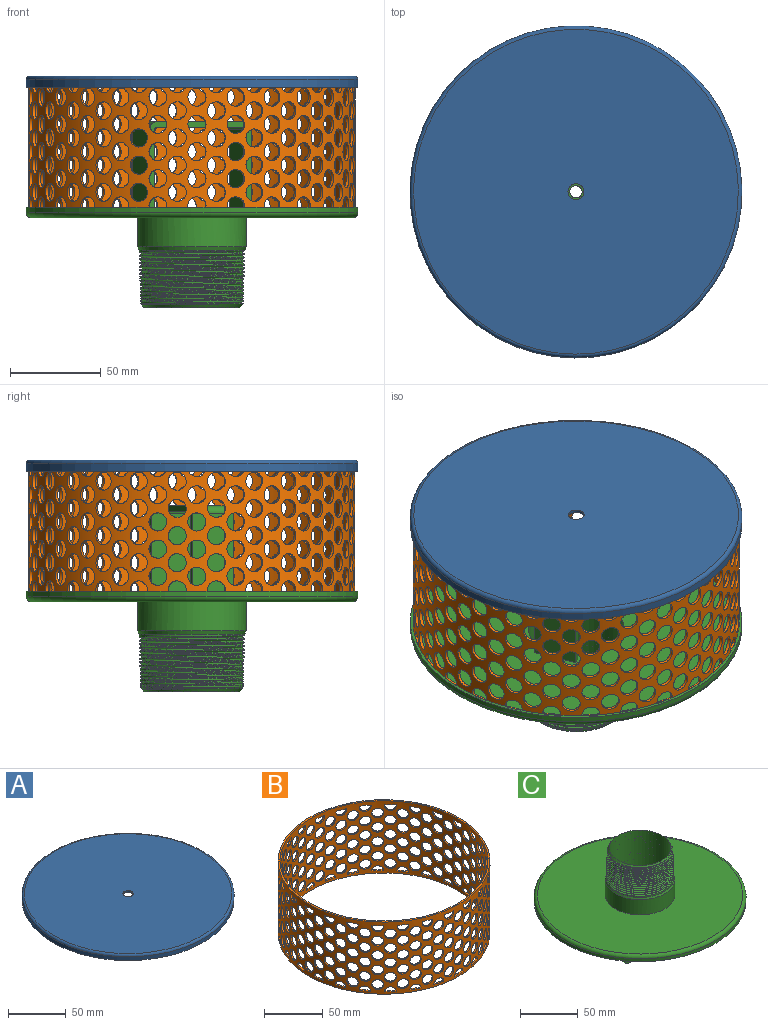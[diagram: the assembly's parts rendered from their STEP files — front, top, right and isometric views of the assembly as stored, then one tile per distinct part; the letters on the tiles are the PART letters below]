
ASSEMBLY  parts=3 mates=4
PART A: 8 faces, bbox 198.3x198.3x6 mm
  f0: cylinder r=91.6mm len=183.2mm, axis (0,0,-1), area 2302.2mm2, adj f2,f3
  f1: plane 179.2x179.2mm, normal (0,0,1), area 25160.4mm2, adj f3,f7
  f2: plane 183.2x183.2mm, normal (0,0,-1), area 912.8mm2, adj f0,f4
  f3: torus R=89.6mm, axis (0,0,1), area 1793.8mm2, adj f0,f1
  f4: cylinder r=90mm len=180mm, axis (0,0,-1), area 2261.9mm2, adj f2,f6
  f5: plane 179.2x179.2mm, normal (0,0,-1), area 25160.4mm2, adj f6,f7
  f6: torus R=89.6mm, axis (0,0,1), area 354.7mm2, adj f4,f5
  f7: cylinder r=4.4mm len=8.8mm, axis (0,0,1), area 44.2mm2, adj f1,f5
PART B: 316 faces, bbox 180x180x75 mm
  f0: cylinder r=90mm len=180mm, axis (0,0,-1), area 23634.4mm2, adj f2,f3,f4,f5,f6,f7,f8,f9
  f1: cylinder r=88.4mm len=176.8mm, axis (0,0,-1), area 22883mm2, adj f2,f3,f4,f5,f6,f7,f8,f9
  f2: plane 180x180mm, normal (0,0,1), area 896.7mm2, adj f0,f1
  f3: plane 180x180mm, normal (0,0,-1), area 896.7mm2, adj f0,f1
  f4: cylinder r=5mm len=10mm, axis (-1,0,0), area 50.3mm2, adj f0,f1
  f5: cylinder r=5mm len=10mm, axis (-1,0,0), area 28.9mm2, adj f0,f1,f6
  f6: plane 9.76x1.74mm, normal (0,0,-1), area 15.6mm2, adj f0,f1,f5
  f7: cylinder r=5mm len=10mm, axis (-1,0,0), area 50.3mm2, adj f0,f1
  f8: cylinder r=5mm len=10mm, axis (-1,0,0), area 50.3mm2, adj f0,f1
  f9: cylinder r=5mm len=10mm, axis (-1,0,0), area 50.3mm2, adj f0,f1
  f10: cylinder r=5mm len=10.13mm, axis (-0.97,-0.24,0), area 50.3mm2, adj f0,f1
  f11: cylinder r=5mm len=10.13mm, axis (-0.97,-0.24,0), area 28.7mm2, adj f0,f1,f12
  f12: plane 9.86x3.89mm, normal (0,0,-1), area 15.6mm2, adj f0,f1,f11
  f13: cylinder r=5mm len=10.13mm, axis (-0.97,-0.24,0), area 50.3mm2, adj f0,f1
  f14: cylinder r=5mm len=10.13mm, axis (-0.97,-0.24,0), area 50.3mm2, adj f0,f1
  f15: cylinder r=5mm len=10.13mm, axis (-0.97,-0.24,0), area 50.3mm2, adj f0,f1
  f16: cylinder r=5mm len=10mm, axis (-0.89,-0.46,0), area 50.3mm2, adj f0,f1
  f17: cylinder r=5mm len=9.66mm, axis (-0.89,-0.46,0), area 28.7mm2, adj f0,f1,f18
  f18: plane 9.39x5.96mm, normal (0,0,-1), area 15.6mm2, adj f0,f1,f17
  f19: cylinder r=5mm len=10mm, axis (-0.89,-0.46,0), area 50.3mm2, adj f0,f1
  f20: cylinder r=5mm len=10mm, axis (-0.89,-0.46,0), area 50.3mm2, adj f0,f1
  f21: cylinder r=5mm len=10mm, axis (-0.89,-0.46,0), area 50.3mm2, adj f0,f1
  f22: cylinder r=5mm len=10mm, axis (-0.75,-0.66,0), area 50.3mm2, adj f0,f1
  f23: cylinder r=5mm len=8.64mm, axis (-0.75,-0.66,0), area 28.7mm2, adj f0,f1,f24
  f24: plane 8.37x7.67mm, normal (0,0,-1), area 15.6mm2, adj f0,f1,f23
  f25: cylinder r=5mm len=10mm, axis (-0.75,-0.66,0), area 50.3mm2, adj f0,f1
  f26: cylinder r=5mm len=10mm, axis (-0.75,-0.66,0), area 50.3mm2, adj f0,f1
  f27: cylinder r=5mm len=10mm, axis (-0.75,-0.66,0), area 50.3mm2, adj f0,f1
  f28: cylinder r=5mm len=10mm, axis (-0.57,-0.82,0), area 50.3mm2, adj f0,f1
  f29: cylinder r=5mm len=9.22mm, axis (-0.57,-0.82,0), area 28.7mm2, adj f0,f1,f30
  f30: plane 8.94x6.86mm, normal (0,0,-1), area 15.6mm2, adj f0,f1,f29
  f31: cylinder r=5mm len=10mm, axis (-0.57,-0.82,0), area 50.3mm2, adj f0,f1
  f32: cylinder r=5mm len=10mm, axis (-0.57,-0.82,0), area 50.3mm2, adj f0,f1
  f33: cylinder r=5mm len=10mm, axis (-0.57,-0.82,0), area 50.3mm2, adj f0,f1
  f34: cylinder r=5mm len=10mm, axis (-0.35,-0.94,0), area 50.3mm2, adj f0,f1
  f35: cylinder r=5mm len=9.97mm, axis (-0.35,-0.94,0), area 28.7mm2, adj f0,f1,f36
  f36: plane 9.7x4.96mm, normal (0,0,-1), area 15.6mm2, adj f0,f1,f35
  f37: cylinder r=5mm len=10mm, axis (-0.35,-0.94,0), area 50.3mm2, adj f0,f1
  f38: cylinder r=5mm len=10mm, axis (-0.35,-0.94,0), area 50.3mm2, adj f0,f1
  f39: cylinder r=5mm len=10mm, axis (-0.35,-0.94,0), area 50.3mm2, adj f0,f1
  f40: cylinder r=5mm len=10.14mm, axis (-0.12,-0.99,0), area 50.3mm2, adj f0,f1
  f41: cylinder r=5mm len=10.14mm, axis (-0.12,-0.99,0), area 28.7mm2, adj f0,f1,f42
  f42: plane 9.88x2.77mm, normal (0,0,-1), area 15.6mm2, adj f0,f1,f41
  f43: cylinder r=5mm len=10.14mm, axis (-0.12,-0.99,0), area 50.3mm2, adj f0,f1
  f44: cylinder r=5mm len=10.14mm, axis (-0.12,-0.99,0), area 50.3mm2, adj f0,f1
  f45: cylinder r=5mm len=10.14mm, axis (-0.12,-0.99,0), area 50.3mm2, adj f0,f1
  f46: cylinder r=5mm len=10.14mm, axis (0.12,-0.99,0), area 50.3mm2, adj f0,f1
  f47: cylinder r=5mm len=10.14mm, axis (0.12,-0.99,0), area 28.7mm2, adj f0,f1,f48
  f48: plane 9.88x2.77mm, normal (0,0,-1), area 15.6mm2, adj f0,f1,f47
  f49: cylinder r=5mm len=10.14mm, axis (0.12,-0.99,0), area 50.3mm2, adj f0,f1
  f50: cylinder r=5mm len=10.14mm, axis (0.12,-0.99,0), area 50.3mm2, adj f0,f1
  f51: cylinder r=5mm len=10.14mm, axis (0.12,-0.99,0), area 50.3mm2, adj f0,f1
  f52: cylinder r=5mm len=10mm, axis (0.35,-0.94,0), area 50.3mm2, adj f0,f1
  f53: cylinder r=5mm len=9.97mm, axis (0.35,-0.94,0), area 28.7mm2, adj f0,f1,f54
  f54: plane 9.7x4.96mm, normal (0,0,-1), area 15.6mm2, adj f0,f1,f53
  f55: cylinder r=5mm len=10mm, axis (0.35,-0.94,0), area 50.3mm2, adj f0,f1
  f56: cylinder r=5mm len=10mm, axis (0.35,-0.94,0), area 50.3mm2, adj f0,f1
  f57: cylinder r=5mm len=10mm, axis (0.35,-0.94,0), area 50.3mm2, adj f0,f1
  f58: cylinder r=5mm len=10mm, axis (0.57,-0.82,0), area 50.3mm2, adj f0,f1
  f59: cylinder r=5mm len=9.22mm, axis (0.57,-0.82,0), area 28.7mm2, adj f0,f1,f60
  f60: plane 8.94x6.86mm, normal (0,0,-1), area 15.6mm2, adj f0,f1,f59
  f61: cylinder r=5mm len=10mm, axis (0.57,-0.82,0), area 50.3mm2, adj f0,f1
  f62: cylinder r=5mm len=10mm, axis (0.57,-0.82,0), area 50.3mm2, adj f0,f1
  f63: cylinder r=5mm len=10mm, axis (0.57,-0.82,0), area 50.3mm2, adj f0,f1
  f64: cylinder r=5mm len=10mm, axis (0.75,-0.66,0), area 50.3mm2, adj f0,f1
  f65: cylinder r=5mm len=8.64mm, axis (0.75,-0.66,0), area 28.7mm2, adj f0,f1,f66
  f66: plane 8.37x7.67mm, normal (0,0,-1), area 15.6mm2, adj f0,f1,f65
  f67: cylinder r=5mm len=10mm, axis (0.75,-0.66,0), area 50.3mm2, adj f0,f1
  f68: cylinder r=5mm len=10mm, axis (0.75,-0.66,0), area 50.3mm2, adj f0,f1
  f69: cylinder r=5mm len=10mm, axis (0.75,-0.66,0), area 50.3mm2, adj f0,f1
  f70: cylinder r=5mm len=10mm, axis (0.89,-0.46,0), area 50.3mm2, adj f0,f1
  f71: cylinder r=5mm len=9.66mm, axis (0.89,-0.46,0), area 28.7mm2, adj f0,f1,f72
  f72: plane 9.39x5.96mm, normal (0,0,-1), area 15.6mm2, adj f0,f1,f71
  f73: cylinder r=5mm len=10mm, axis (0.89,-0.46,0), area 50.3mm2, adj f0,f1
  f74: cylinder r=5mm len=10mm, axis (0.89,-0.46,0), area 50.3mm2, adj f0,f1
  f75: cylinder r=5mm len=10mm, axis (0.89,-0.46,0), area 50.3mm2, adj f0,f1
  f76: cylinder r=5mm len=10.13mm, axis (0.97,-0.24,0), area 50.3mm2, adj f0,f1
  f77: cylinder r=5mm len=10.13mm, axis (0.97,-0.24,0), area 28.7mm2, adj f0,f1,f78
  f78: plane 9.86x3.89mm, normal (0,0,-1), area 15.6mm2, adj f0,f1,f77
  f79: cylinder r=5mm len=10.13mm, axis (0.97,-0.24,0), area 50.3mm2, adj f0,f1
  f80: cylinder r=5mm len=10.13mm, axis (0.97,-0.24,0), area 50.3mm2, adj f0,f1
  f81: cylinder r=5mm len=10.13mm, axis (0.97,-0.24,0), area 50.3mm2, adj f0,f1
  f82: cylinder r=5mm len=10mm, axis (1,0,0), area 50.3mm2, adj f0,f1
  f83: cylinder r=5mm len=10mm, axis (1,0,0), area 28.7mm2, adj f0,f1,f84
  f84: plane 9.76x1.74mm, normal (0,0,-1), area 15.6mm2, adj f0,f1,f83
  f85: cylinder r=5mm len=10mm, axis (1,0,0), area 50.3mm2, adj f0,f1
  f86: cylinder r=5mm len=10mm, axis (1,0,0), area 50.3mm2, adj f0,f1
  f87: cylinder r=5mm len=10mm, axis (1,0,0), area 50.3mm2, adj f0,f1
  f88: cylinder r=5mm len=10.13mm, axis (0.97,0.24,0), area 50.3mm2, adj f0,f1
  f89: cylinder r=5mm len=10.13mm, axis (0.97,0.24,0), area 28.7mm2, adj f0,f1,f90
  f90: plane 9.86x3.89mm, normal (0,0,-1), area 15.6mm2, adj f0,f1,f89
  f91: cylinder r=5mm len=10.13mm, axis (0.97,0.24,0), area 50.3mm2, adj f0,f1
  f92: cylinder r=5mm len=10.13mm, axis (0.97,0.24,0), area 50.3mm2, adj f0,f1
  f93: cylinder r=5mm len=10.13mm, axis (0.97,0.24,0), area 50.3mm2, adj f0,f1
  f94: cylinder r=5mm len=10mm, axis (0.89,0.46,0), area 50.3mm2, adj f0,f1
  f95: cylinder r=5mm len=9.66mm, axis (0.89,0.46,0), area 28.7mm2, adj f0,f1,f96
  f96: plane 9.39x5.96mm, normal (0,0,-1), area 15.6mm2, adj f0,f1,f95
  f97: cylinder r=5mm len=10mm, axis (0.89,0.46,0), area 50.3mm2, adj f0,f1
  f98: cylinder r=5mm len=10mm, axis (0.89,0.46,0), area 50.3mm2, adj f0,f1
  f99: cylinder r=5mm len=10mm, axis (0.89,0.46,0), area 50.3mm2, adj f0,f1
  f100: cylinder r=5mm len=10mm, axis (0.75,0.66,0), area 50.3mm2, adj f0,f1
  f101: cylinder r=5mm len=8.64mm, axis (0.75,0.66,0), area 28.7mm2, adj f0,f1,f102
  f102: plane 8.37x7.67mm, normal (0,0,-1), area 15.6mm2, adj f0,f1,f101
  f103: cylinder r=5mm len=10mm, axis (0.75,0.66,0), area 50.3mm2, adj f0,f1
  f104: cylinder r=5mm len=10mm, axis (0.75,0.66,0), area 50.3mm2, adj f0,f1
  f105: cylinder r=5mm len=10mm, axis (0.75,0.66,0), area 50.3mm2, adj f0,f1
  f106: cylinder r=5mm len=10mm, axis (0.57,0.82,0), area 50.3mm2, adj f0,f1
  f107: cylinder r=5mm len=9.22mm, axis (0.57,0.82,0), area 28.7mm2, adj f0,f1,f108
  f108: plane 8.94x6.86mm, normal (0,0,-1), area 15.6mm2, adj f0,f1,f107
  f109: cylinder r=5mm len=10mm, axis (0.57,0.82,0), area 50.3mm2, adj f0,f1
  f110: cylinder r=5mm len=10mm, axis (0.57,0.82,0), area 50.3mm2, adj f0,f1
  f111: cylinder r=5mm len=10mm, axis (0.57,0.82,0), area 50.3mm2, adj f0,f1
  f112: cylinder r=5mm len=10mm, axis (0.35,0.94,0), area 50.3mm2, adj f0,f1
  f113: cylinder r=5mm len=9.97mm, axis (0.35,0.94,0), area 28.7mm2, adj f0,f1,f114
  f114: plane 9.7x4.96mm, normal (0,0,-1), area 15.6mm2, adj f0,f1,f113
  f115: cylinder r=5mm len=10mm, axis (0.35,0.94,0), area 50.3mm2, adj f0,f1
  f116: cylinder r=5mm len=10mm, axis (0.35,0.94,0), area 50.3mm2, adj f0,f1
  f117: cylinder r=5mm len=10mm, axis (0.35,0.94,0), area 50.3mm2, adj f0,f1
  f118: cylinder r=5mm len=10.14mm, axis (0.12,0.99,0), area 50.3mm2, adj f0,f1
  f119: cylinder r=5mm len=10.14mm, axis (0.12,0.99,0), area 28.7mm2, adj f0,f1,f120
  f120: plane 9.88x2.77mm, normal (0,0,-1), area 15.6mm2, adj f0,f1,f119
  f121: cylinder r=5mm len=10.14mm, axis (0.12,0.99,0), area 50.3mm2, adj f0,f1
  f122: cylinder r=5mm len=10.14mm, axis (0.12,0.99,0), area 50.3mm2, adj f0,f1
  f123: cylinder r=5mm len=10.14mm, axis (0.12,0.99,0), area 50.3mm2, adj f0,f1
  f124: cylinder r=5mm len=10.14mm, axis (-0.12,0.99,0), area 50.3mm2, adj f0,f1
  f125: cylinder r=5mm len=10.14mm, axis (-0.12,0.99,0), area 28.7mm2, adj f0,f1,f126
  f126: plane 9.88x2.77mm, normal (0,0,-1), area 15.6mm2, adj f0,f1,f125
  f127: cylinder r=5mm len=10.14mm, axis (-0.12,0.99,0), area 50.3mm2, adj f0,f1
  f128: cylinder r=5mm len=10.14mm, axis (-0.12,0.99,0), area 50.3mm2, adj f0,f1
  f129: cylinder r=5mm len=10.14mm, axis (-0.12,0.99,0), area 50.3mm2, adj f0,f1
  f130: cylinder r=5mm len=10mm, axis (-0.35,0.94,0), area 50.3mm2, adj f0,f1
  f131: cylinder r=5mm len=9.97mm, axis (-0.35,0.94,0), area 28.7mm2, adj f0,f1,f132
  f132: plane 9.7x4.96mm, normal (0,0,-1), area 15.6mm2, adj f0,f1,f131
  f133: cylinder r=5mm len=10mm, axis (-0.35,0.94,0), area 50.3mm2, adj f0,f1
  f134: cylinder r=5mm len=10mm, axis (-0.35,0.94,0), area 50.3mm2, adj f0,f1
  f135: cylinder r=5mm len=10mm, axis (-0.35,0.94,0), area 50.3mm2, adj f0,f1
  f136: cylinder r=5mm len=10mm, axis (-0.57,0.82,0), area 50.3mm2, adj f0,f1
  f137: cylinder r=5mm len=9.22mm, axis (-0.57,0.82,0), area 28.7mm2, adj f0,f1,f138
  f138: plane 8.94x6.86mm, normal (0,0,-1), area 15.6mm2, adj f0,f1,f137
  f139: cylinder r=5mm len=10mm, axis (-0.57,0.82,0), area 50.3mm2, adj f0,f1
  f140: cylinder r=5mm len=10mm, axis (-0.57,0.82,0), area 50.3mm2, adj f0,f1
  f141: cylinder r=5mm len=10mm, axis (-0.57,0.82,0), area 50.3mm2, adj f0,f1
  f142: cylinder r=5mm len=10mm, axis (-0.75,0.66,0), area 50.3mm2, adj f0,f1
  f143: cylinder r=5mm len=8.64mm, axis (-0.75,0.66,0), area 28.7mm2, adj f0,f1,f144
  f144: plane 8.37x7.67mm, normal (0,0,-1), area 15.6mm2, adj f0,f1,f143
  f145: cylinder r=5mm len=10mm, axis (-0.75,0.66,0), area 50.3mm2, adj f0,f1
  f146: cylinder r=5mm len=10mm, axis (-0.75,0.66,0), area 50.3mm2, adj f0,f1
  f147: cylinder r=5mm len=10mm, axis (-0.75,0.66,0), area 50.3mm2, adj f0,f1
  f148: cylinder r=5mm len=10mm, axis (-0.89,0.46,0), area 50.3mm2, adj f0,f1
  f149: cylinder r=5mm len=9.66mm, axis (-0.89,0.46,0), area 28.7mm2, adj f0,f1,f150
  f150: plane 9.39x5.96mm, normal (0,0,-1), area 15.6mm2, adj f0,f1,f149
  f151: cylinder r=5mm len=10mm, axis (-0.89,0.46,0), area 50.3mm2, adj f0,f1
  f152: cylinder r=5mm len=10mm, axis (-0.89,0.46,0), area 50.3mm2, adj f0,f1
  f153: cylinder r=5mm len=10mm, axis (-0.89,0.46,0), area 50.3mm2, adj f0,f1
  f154: cylinder r=5mm len=10.13mm, axis (-0.97,0.24,0), area 50.3mm2, adj f0,f1
  f155: cylinder r=5mm len=10.13mm, axis (-0.97,0.24,0), area 28.7mm2, adj f0,f1,f156
  f156: plane 9.86x3.89mm, normal (0,0,-1), area 15.6mm2, adj f0,f1,f155
  f157: cylinder r=5mm len=10.13mm, axis (-0.97,0.24,0), area 50.3mm2, adj f0,f1
  f158: cylinder r=5mm len=10.13mm, axis (-0.97,0.24,0), area 50.3mm2, adj f0,f1
  f159: cylinder r=5mm len=10.13mm, axis (-0.97,0.24,0), area 50.3mm2, adj f0,f1
  f160: cylinder r=5mm len=10mm, axis (0,1,0), area 50.3mm2, adj f0,f1
  f161: cylinder r=5mm len=10mm, axis (0,1,0), area 50.3mm2, adj f0,f1
  f162: cylinder r=5mm len=10mm, axis (0,1,0), area 50.3mm2, adj f0,f1
  f163: cylinder r=5mm len=10mm, axis (0,1,0), area 50.3mm2, adj f0,f1
  f164: plane 10x1.74mm, normal (0,0,1), area 16mm2, adj f0,f1,f165
  f165: cylinder r=5mm len=10mm, axis (0,1,0), area 25.2mm2, adj f0,f1,f164
  f166: cylinder r=5mm len=10.13mm, axis (-0.24,0.97,0), area 50.3mm2, adj f0,f1
  f167: cylinder r=5mm len=10.13mm, axis (-0.24,0.97,0), area 50.3mm2, adj f0,f1
  f168: cylinder r=5mm len=10.13mm, axis (-0.24,0.97,0), area 50.3mm2, adj f0,f1
  f169: cylinder r=5mm len=10.13mm, axis (-0.24,0.97,0), area 50.3mm2, adj f0,f1
  f170: plane 10.09x3.95mm, normal (0,0,1), area 16mm2, adj f0,f1,f171
  f171: cylinder r=5mm len=10.13mm, axis (-0.24,0.97,0), area 25.2mm2, adj f0,f1,f170
  f172: cylinder r=5mm len=10mm, axis (-0.46,0.89,0), area 50.3mm2, adj f0,f1
  f173: cylinder r=5mm len=10mm, axis (-0.46,0.89,0), area 50.3mm2, adj f0,f1
  f174: cylinder r=5mm len=10mm, axis (-0.46,0.89,0), area 50.3mm2, adj f0,f1
  f175: cylinder r=5mm len=10mm, axis (-0.46,0.89,0), area 50.3mm2, adj f0,f1
  f176: plane 9.6x6.07mm, normal (0,0,1), area 16mm2, adj f0,f1,f177
  f177: cylinder r=5mm len=9.66mm, axis (-0.46,0.89,0), area 25.2mm2, adj f0,f1,f176
  f178: cylinder r=5mm len=10mm, axis (-0.66,0.75,0), area 50.3mm2, adj f0,f1
  f179: cylinder r=5mm len=10mm, axis (-0.66,0.75,0), area 50.3mm2, adj f0,f1
  f180: cylinder r=5mm len=10mm, axis (-0.66,0.75,0), area 50.3mm2, adj f0,f1
  f181: cylinder r=5mm len=10mm, axis (-0.66,0.75,0), area 50.3mm2, adj f0,f1
  f182: plane 8.55x7.83mm, normal (0,0,1), area 16mm2, adj f0,f1,f183
  f183: cylinder r=5mm len=8.64mm, axis (-0.66,0.75,0), area 25.2mm2, adj f0,f1,f182
  f184: cylinder r=5mm len=10mm, axis (-0.82,0.57,0), area 50.3mm2, adj f0,f1
  f185: cylinder r=5mm len=10mm, axis (-0.82,0.57,0), area 50.3mm2, adj f0,f1
  f186: cylinder r=5mm len=10mm, axis (-0.82,0.57,0), area 50.3mm2, adj f0,f1
  f187: cylinder r=5mm len=10mm, axis (-0.82,0.57,0), area 50.3mm2, adj f0,f1
  f188: plane 9.14x7mm, normal (0,0,1), area 16mm2, adj f0,f1,f189
  f189: cylinder r=5mm len=9.22mm, axis (-0.82,0.57,0), area 25.2mm2, adj f0,f1,f188
  f190: cylinder r=5mm len=10mm, axis (-0.94,0.35,0), area 50.3mm2, adj f0,f1
  f191: cylinder r=5mm len=10mm, axis (-0.94,0.35,0), area 50.3mm2, adj f0,f1
  f192: cylinder r=5mm len=10mm, axis (-0.94,0.35,0), area 50.3mm2, adj f0,f1
  f193: cylinder r=5mm len=10mm, axis (-0.94,0.35,0), area 50.3mm2, adj f0,f1
  f194: plane 9.92x5.04mm, normal (0,0,1), area 16mm2, adj f0,f1,f195
  f195: cylinder r=5mm len=9.97mm, axis (-0.94,0.35,0), area 25.2mm2, adj f0,f1,f194
  f196: cylinder r=5mm len=10.14mm, axis (-0.99,0.12,0), area 50.3mm2, adj f0,f1
  f197: cylinder r=5mm len=10.14mm, axis (-0.99,0.12,0), area 50.3mm2, adj f0,f1
  f198: cylinder r=5mm len=10.14mm, axis (-0.99,0.12,0), area 50.3mm2, adj f0,f1
  f199: cylinder r=5mm len=10.14mm, axis (-0.99,0.12,0), area 50.3mm2, adj f0,f1
  f200: plane 10.12x2.8mm, normal (0,0,1), area 16mm2, adj f0,f1,f201
  f201: cylinder r=5mm len=10.14mm, axis (-0.99,0.12,0), area 25.2mm2, adj f0,f1,f200
  f202: cylinder r=5mm len=10.14mm, axis (-0.99,-0.12,0), area 50.3mm2, adj f0,f1
  f203: cylinder r=5mm len=10.14mm, axis (-0.99,-0.12,0), area 50.3mm2, adj f0,f1
  f204: cylinder r=5mm len=10.14mm, axis (-0.99,-0.12,0), area 50.3mm2, adj f0,f1
  f205: cylinder r=5mm len=10.14mm, axis (-0.99,-0.12,0), area 50.3mm2, adj f0,f1
  f206: plane 10.12x2.8mm, normal (0,0,1), area 16mm2, adj f0,f1,f207
  f207: cylinder r=5mm len=10.14mm, axis (-0.99,-0.12,0), area 25.2mm2, adj f0,f1,f206
  f208: cylinder r=5mm len=10mm, axis (-0.94,-0.35,0), area 50.3mm2, adj f0,f1
  f209: cylinder r=5mm len=10mm, axis (-0.94,-0.35,0), area 50.3mm2, adj f0,f1
  f210: cylinder r=5mm len=10mm, axis (-0.94,-0.35,0), area 50.3mm2, adj f0,f1
  f211: cylinder r=5mm len=10mm, axis (-0.94,-0.35,0), area 50.3mm2, adj f0,f1
  f212: plane 9.92x5.04mm, normal (0,0,1), area 16mm2, adj f0,f1,f213
  f213: cylinder r=5mm len=9.97mm, axis (-0.94,-0.35,0), area 25.2mm2, adj f0,f1,f212
  f214: cylinder r=5mm len=10mm, axis (-0.82,-0.57,0), area 50.3mm2, adj f0,f1
  f215: cylinder r=5mm len=10mm, axis (-0.82,-0.57,0), area 50.3mm2, adj f0,f1
  f216: cylinder r=5mm len=10mm, axis (-0.82,-0.57,0), area 50.3mm2, adj f0,f1
  f217: cylinder r=5mm len=10mm, axis (-0.82,-0.57,0), area 50.3mm2, adj f0,f1
  f218: plane 9.14x7mm, normal (0,0,1), area 16mm2, adj f0,f1,f219
  f219: cylinder r=5mm len=9.22mm, axis (-0.82,-0.57,0), area 25.2mm2, adj f0,f1,f218
  f220: cylinder r=5mm len=10mm, axis (-0.66,-0.75,0), area 50.3mm2, adj f0,f1
  f221: cylinder r=5mm len=10mm, axis (-0.66,-0.75,0), area 50.3mm2, adj f0,f1
  f222: cylinder r=5mm len=10mm, axis (-0.66,-0.75,0), area 50.3mm2, adj f0,f1
  f223: cylinder r=5mm len=10mm, axis (-0.66,-0.75,0), area 50.3mm2, adj f0,f1
  f224: plane 8.55x7.83mm, normal (0,0,1), area 16mm2, adj f0,f1,f225
  f225: cylinder r=5mm len=8.64mm, axis (-0.66,-0.75,0), area 25.2mm2, adj f0,f1,f224
  f226: cylinder r=5mm len=10mm, axis (-0.46,-0.89,0), area 50.3mm2, adj f0,f1
  f227: cylinder r=5mm len=10mm, axis (-0.46,-0.89,0), area 50.3mm2, adj f0,f1
  f228: cylinder r=5mm len=10mm, axis (-0.46,-0.89,0), area 50.3mm2, adj f0,f1
  f229: cylinder r=5mm len=10mm, axis (-0.46,-0.89,0), area 50.3mm2, adj f0,f1
  f230: plane 9.6x6.07mm, normal (0,0,1), area 16mm2, adj f0,f1,f231
  f231: cylinder r=5mm len=9.66mm, axis (-0.46,-0.89,0), area 25.2mm2, adj f0,f1,f230
  f232: cylinder r=5mm len=10.13mm, axis (-0.24,-0.97,0), area 50.3mm2, adj f0,f1
  f233: cylinder r=5mm len=10.13mm, axis (-0.24,-0.97,0), area 50.3mm2, adj f0,f1
  f234: cylinder r=5mm len=10.13mm, axis (-0.24,-0.97,0), area 50.3mm2, adj f0,f1
  f235: cylinder r=5mm len=10.13mm, axis (-0.24,-0.97,0), area 50.3mm2, adj f0,f1
  f236: plane 10.09x3.95mm, normal (0,0,1), area 16mm2, adj f0,f1,f237
  f237: cylinder r=5mm len=10.13mm, axis (-0.24,-0.97,0), area 25.2mm2, adj f0,f1,f236
  f238: cylinder r=5mm len=10mm, axis (0,-1,0), area 50.3mm2, adj f0,f1
  f239: cylinder r=5mm len=10mm, axis (0,-1,0), area 50.3mm2, adj f0,f1
  f240: cylinder r=5mm len=10mm, axis (0,-1,0), area 50.3mm2, adj f0,f1
  f241: cylinder r=5mm len=10mm, axis (0,-1,0), area 50.3mm2, adj f0,f1
  f242: plane 10x1.74mm, normal (0,0,1), area 16mm2, adj f0,f1,f243
  f243: cylinder r=5mm len=10mm, axis (0,-1,0), area 25.2mm2, adj f0,f1,f242
  f244: cylinder r=5mm len=10.13mm, axis (0.24,-0.97,0), area 50.3mm2, adj f0,f1
  f245: cylinder r=5mm len=10.13mm, axis (0.24,-0.97,0), area 50.3mm2, adj f0,f1
  f246: cylinder r=5mm len=10.13mm, axis (0.24,-0.97,0), area 50.3mm2, adj f0,f1
  f247: cylinder r=5mm len=10.13mm, axis (0.24,-0.97,0), area 50.3mm2, adj f0,f1
  f248: plane 10.09x3.95mm, normal (0,0,1), area 16mm2, adj f0,f1,f249
  f249: cylinder r=5mm len=10.13mm, axis (0.24,-0.97,0), area 25.2mm2, adj f0,f1,f248
  f250: cylinder r=5mm len=10mm, axis (0.46,-0.89,0), area 50.3mm2, adj f0,f1
  f251: cylinder r=5mm len=10mm, axis (0.46,-0.89,0), area 50.3mm2, adj f0,f1
  f252: cylinder r=5mm len=10mm, axis (0.46,-0.89,0), area 50.3mm2, adj f0,f1
  f253: cylinder r=5mm len=10mm, axis (0.46,-0.89,0), area 50.3mm2, adj f0,f1
  f254: plane 9.6x6.07mm, normal (0,0,1), area 16mm2, adj f0,f1,f255
  f255: cylinder r=5mm len=9.66mm, axis (0.46,-0.89,0), area 25.2mm2, adj f0,f1,f254
  f256: cylinder r=5mm len=10mm, axis (0.66,-0.75,0), area 50.3mm2, adj f0,f1
  f257: cylinder r=5mm len=10mm, axis (0.66,-0.75,0), area 50.3mm2, adj f0,f1
  f258: cylinder r=5mm len=10mm, axis (0.66,-0.75,0), area 50.3mm2, adj f0,f1
  f259: cylinder r=5mm len=10mm, axis (0.66,-0.75,0), area 50.3mm2, adj f0,f1
  f260: plane 8.55x7.83mm, normal (0,0,1), area 16mm2, adj f0,f1,f261
  f261: cylinder r=5mm len=8.64mm, axis (0.66,-0.75,0), area 25.2mm2, adj f0,f1,f260
  f262: cylinder r=5mm len=10mm, axis (0.82,-0.57,0), area 50.3mm2, adj f0,f1
  f263: cylinder r=5mm len=10mm, axis (0.82,-0.57,0), area 50.3mm2, adj f0,f1
  f264: cylinder r=5mm len=10mm, axis (0.82,-0.57,0), area 50.3mm2, adj f0,f1
  f265: cylinder r=5mm len=10mm, axis (0.82,-0.57,0), area 50.3mm2, adj f0,f1
  f266: plane 9.14x7mm, normal (0,0,1), area 16mm2, adj f0,f1,f267
  f267: cylinder r=5mm len=9.22mm, axis (0.82,-0.57,0), area 25.2mm2, adj f0,f1,f266
  f268: cylinder r=5mm len=10mm, axis (0.94,-0.35,0), area 50.3mm2, adj f0,f1
  f269: cylinder r=5mm len=10mm, axis (0.94,-0.35,0), area 50.3mm2, adj f0,f1
  f270: cylinder r=5mm len=10mm, axis (0.94,-0.35,0), area 50.3mm2, adj f0,f1
  f271: cylinder r=5mm len=10mm, axis (0.94,-0.35,0), area 50.3mm2, adj f0,f1
  f272: plane 9.92x5.04mm, normal (0,0,1), area 16mm2, adj f0,f1,f273
  f273: cylinder r=5mm len=9.97mm, axis (0.94,-0.35,0), area 25.2mm2, adj f0,f1,f272
  f274: cylinder r=5mm len=10.14mm, axis (0.99,-0.12,0), area 50.3mm2, adj f0,f1
  f275: cylinder r=5mm len=10.14mm, axis (0.99,-0.12,0), area 50.3mm2, adj f0,f1
  f276: cylinder r=5mm len=10.14mm, axis (0.99,-0.12,0), area 50.3mm2, adj f0,f1
  f277: cylinder r=5mm len=10.14mm, axis (0.99,-0.12,0), area 50.3mm2, adj f0,f1
  f278: plane 10.12x2.8mm, normal (0,0,1), area 16mm2, adj f0,f1,f279
  f279: cylinder r=5mm len=10.14mm, axis (0.99,-0.12,0), area 25.2mm2, adj f0,f1,f278
  f280: cylinder r=5mm len=10.14mm, axis (0.99,0.12,0), area 50.3mm2, adj f0,f1
  f281: cylinder r=5mm len=10.14mm, axis (0.99,0.12,0), area 50.3mm2, adj f0,f1
  f282: cylinder r=5mm len=10.14mm, axis (0.99,0.12,0), area 50.3mm2, adj f0,f1
  f283: cylinder r=5mm len=10.14mm, axis (0.99,0.12,0), area 50.3mm2, adj f0,f1
  f284: plane 10.12x2.8mm, normal (0,0,1), area 16mm2, adj f0,f1,f285
  f285: cylinder r=5mm len=10.14mm, axis (0.99,0.12,0), area 25.2mm2, adj f0,f1,f284
  f286: cylinder r=5mm len=10mm, axis (0.94,0.35,0), area 50.3mm2, adj f0,f1
  f287: cylinder r=5mm len=10mm, axis (0.94,0.35,0), area 50.3mm2, adj f0,f1
  f288: cylinder r=5mm len=10mm, axis (0.94,0.35,0), area 50.3mm2, adj f0,f1
  f289: cylinder r=5mm len=10mm, axis (0.94,0.35,0), area 50.3mm2, adj f0,f1
  f290: plane 9.92x5.04mm, normal (0,0,1), area 16mm2, adj f0,f1,f291
  f291: cylinder r=5mm len=9.97mm, axis (0.94,0.35,0), area 25.2mm2, adj f0,f1,f290
  f292: cylinder r=5mm len=10mm, axis (0.82,0.57,0), area 50.3mm2, adj f0,f1
  f293: cylinder r=5mm len=10mm, axis (0.82,0.57,0), area 50.3mm2, adj f0,f1
  f294: cylinder r=5mm len=10mm, axis (0.82,0.57,0), area 50.3mm2, adj f0,f1
  f295: cylinder r=5mm len=10mm, axis (0.82,0.57,0), area 50.3mm2, adj f0,f1
  f296: plane 9.14x7mm, normal (0,0,1), area 16mm2, adj f0,f1,f297
  f297: cylinder r=5mm len=9.22mm, axis (0.82,0.57,0), area 25.2mm2, adj f0,f1,f296
  f298: cylinder r=5mm len=10mm, axis (0.66,0.75,0), area 50.3mm2, adj f0,f1
  f299: cylinder r=5mm len=10mm, axis (0.66,0.75,0), area 50.3mm2, adj f0,f1
  f300: cylinder r=5mm len=10mm, axis (0.66,0.75,0), area 50.3mm2, adj f0,f1
  f301: cylinder r=5mm len=10mm, axis (0.66,0.75,0), area 50.3mm2, adj f0,f1
  f302: plane 8.55x7.83mm, normal (0,0,1), area 16mm2, adj f0,f1,f303
  f303: cylinder r=5mm len=8.64mm, axis (0.66,0.75,0), area 25.2mm2, adj f0,f1,f302
  f304: cylinder r=5mm len=10mm, axis (0.46,0.89,0), area 50.3mm2, adj f0,f1
  f305: cylinder r=5mm len=10mm, axis (0.46,0.89,0), area 50.3mm2, adj f0,f1
  f306: cylinder r=5mm len=10mm, axis (0.46,0.89,0), area 50.3mm2, adj f0,f1
  f307: cylinder r=5mm len=10mm, axis (0.46,0.89,0), area 50.3mm2, adj f0,f1
  f308: plane 9.6x6.07mm, normal (0,0,1), area 16mm2, adj f0,f1,f309
  f309: cylinder r=5mm len=9.66mm, axis (0.46,0.89,0), area 25.2mm2, adj f0,f1,f308
  f310: cylinder r=5mm len=10.13mm, axis (0.24,0.97,0), area 50.3mm2, adj f0,f1
  f311: cylinder r=5mm len=10.13mm, axis (0.24,0.97,0), area 50.3mm2, adj f0,f1
  f312: cylinder r=5mm len=10.13mm, axis (0.24,0.97,0), area 50.3mm2, adj f0,f1
  f313: cylinder r=5mm len=10.13mm, axis (0.24,0.97,0), area 50.3mm2, adj f0,f1
  f314: plane 10.09x3.95mm, normal (0,0,1), area 16mm2, adj f0,f1,f315
  f315: cylinder r=5mm len=10.13mm, axis (0.24,0.97,0), area 25.2mm2, adj f0,f1,f314
PART C: 43 faces, bbox 198.3x198.3x102.8 mm
  f0: cylinder r=30mm len=60mm, axis (0,0,-1), area 3020.2mm2, adj f3,f9
  f1: cylinder r=26.5mm len=53mm, axis (0,0,1), area 8531.2mm2, adj f7,f10
  f2: cylinder r=91.6mm len=183.2mm, axis (0,0,-1), area 1726.6mm2, adj f4,f5
  f3: plane 177.2x177.2mm, normal (0,0,1), area 21833.9mm2, adj f0,f5
  f4: plane 183.2x183.2mm, normal (0,0,-1), area 912.8mm2, adj f2,f6
  f5: torus R=88.6mm, axis (0,0,1), area 2679.9mm2, adj f2,f3
  f6: cylinder r=90mm len=180mm, axis (0,0,-1), area 1696.5mm2, adj f4,f8
  f7: plane 177.2x177.2mm, normal (0,0,-1), area 22305.2mm2, adj f1,f8,f30,f31,f32,f33,f34,f35
  f8: torus R=88.6mm, axis (0,0,1), area 1236.5mm2, adj f6,f7
  f9: cone r=30.02mm half-angle=25.6deg, axis (0,0,-1), area 358.7mm2, adj f0,f12
  f10: cone r=28.33mm half-angle=35.3deg, axis (0,0,-1), area 457.8mm2, adj f1,f11,f26,f27,f28
  f11: cone r=28.33mm half-angle=35.3deg, axis (0,0,-1), area 2.4mm2, adj f10,f13,f28
  f12: cone r=29.17mm half-angle=1.6deg, axis (0,0,-1), area 236.6mm2, adj f9,f25,f27,f28,f29
  f13: cone r=29.17mm half-angle=1.6deg, axis (0,0,-1), area 171.8mm2, adj f11,f14,f26,f27,f28
  f14: cone r=29.17mm half-angle=1.6deg, axis (0,0,-1), area 164.5mm2, adj f13,f15,f27,f28
  f15: cone r=29.17mm half-angle=1.6deg, axis (0,0,-1), area 155.8mm2, adj f14,f16,f27,f28
  f16: cone r=29.17mm half-angle=1.6deg, axis (0,0,-1), area 147mm2, adj f15,f17,f27,f28
  f17: cone r=29.17mm half-angle=1.6deg, axis (0,0,-1), area 138.2mm2, adj f16,f18,f27,f28
  f18: cone r=29.17mm half-angle=1.6deg, axis (0,0,-1), area 129.4mm2, adj f17,f19,f27,f28
  f19: cone r=29.17mm half-angle=1.6deg, axis (0,0,-1), area 120.5mm2, adj f18,f20,f27,f28
  f20: cone r=29.17mm half-angle=1.6deg, axis (0,0,-1), area 111.6mm2, adj f19,f21,f27,f28
  f21: cone r=29.17mm half-angle=1.6deg, axis (0,0,-1), area 102.6mm2, adj f20,f22,f27,f28
  f22: cone r=29.17mm half-angle=1.6deg, axis (0,0,-1), area 93.7mm2, adj f21,f23,f27,f28
  f23: cone r=29.17mm half-angle=1.6deg, axis (0,0,-1), area 84.6mm2, adj f22,f24,f27,f28
  f24: cone r=29.17mm half-angle=1.6deg, axis (0,0,-1), area 75.6mm2, adj f23,f25,f27,f28
  f25: cone r=29.17mm half-angle=1.6deg, axis (0,0,-1), area 66.5mm2, adj f12,f24,f27,f28
  f26: cone r=29.17mm half-angle=1.6deg, axis (0,0,-1), area 30.2mm2, adj f10,f13,f27
  f27: bspline ~68.05x58.93mm, area 4195.9mm2, adj f10,f12,f13,f14,f15,f16,f17,f18
  f28: bspline ~68.05x58.93mm, area 4295.6mm2, adj f10,f11,f12,f13,f14,f15,f16,f17
  f29: plane 1.96x1.71mm, normal (0,1,0), area 1.7mm2, adj f12,f27,f28
  f30: plane 47.4x25mm, normal (-1,0,0), area 1185mm2, adj f7,f34,f35,f36
  f31: plane 47.4x25mm, normal (1,0,0), area 1185mm2, adj f7,f34,f35,f38
  f32: plane 47.4x25mm, normal (-1,0,0), area 1185mm2, adj f7,f34,f35,f39
  f33: plane 47.4x25mm, normal (1,0,0), area 1185mm2, adj f7,f34,f35,f41
  f34: plane 61x51.4mm, normal (0,-1,0), area 467mm2, adj f7,f30,f31,f32,f33,f36,f37,f38
  f35: plane 61x51.4mm, normal (0,1,0), area 467mm2, adj f7,f30,f31,f32,f33,f36,f37,f38
  f36: cylinder r=1mm len=25mm, axis (0,1,0), area 39.3mm2, adj f30,f34,f35,f37
  f37: plane 53x25mm, normal (0,0,1), area 1288.7mm2, adj f34,f35,f36,f38,f42
  f38: cylinder r=1mm len=25mm, axis (0,1,0), area 39.3mm2, adj f31,f34,f35,f37
  f39: cylinder r=4mm len=25mm, axis (0,1,0), area 157.1mm2, adj f32,f34,f35,f40
  f40: plane 53x25mm, normal (0,0,-1), area 1288.7mm2, adj f34,f35,f39,f41,f42
  f41: cylinder r=4mm len=25mm, axis (0,1,0), area 157.1mm2, adj f33,f34,f35,f40
  f42: cylinder r=3.4mm len=6.8mm, axis (0,0,-1), area 64.1mm2, adj f37,f40
PLACE A rot(axis=(0,0,1),22.5deg) t=(5.3,9.98,14.42)mm
PLACE B rot(axis=(-0.2,0.98,0),180deg) t=(5.3,9.98,-18.68)mm
PLACE C rot(axis=(-0.98,-0.2,0),180deg) t=(5.3,9.98,-51.78)mm
MATE planar C.f0 <-> B.f0  axis (0,0,1) through (5.3,9.98,-56.18)mm
MATE cylindrical B.f0 <-> C.f0  axis (0,0,1) through (5.3,9.98,-18.68)mm
MATE cylindrical C.f0 <-> A.f0  axis (0,0,-1) through (5.3,9.98,-107.42)mm
MATE planar A.f0 <-> B.f0  axis (0,0,-1) through (5.3,9.98,18.82)mm
